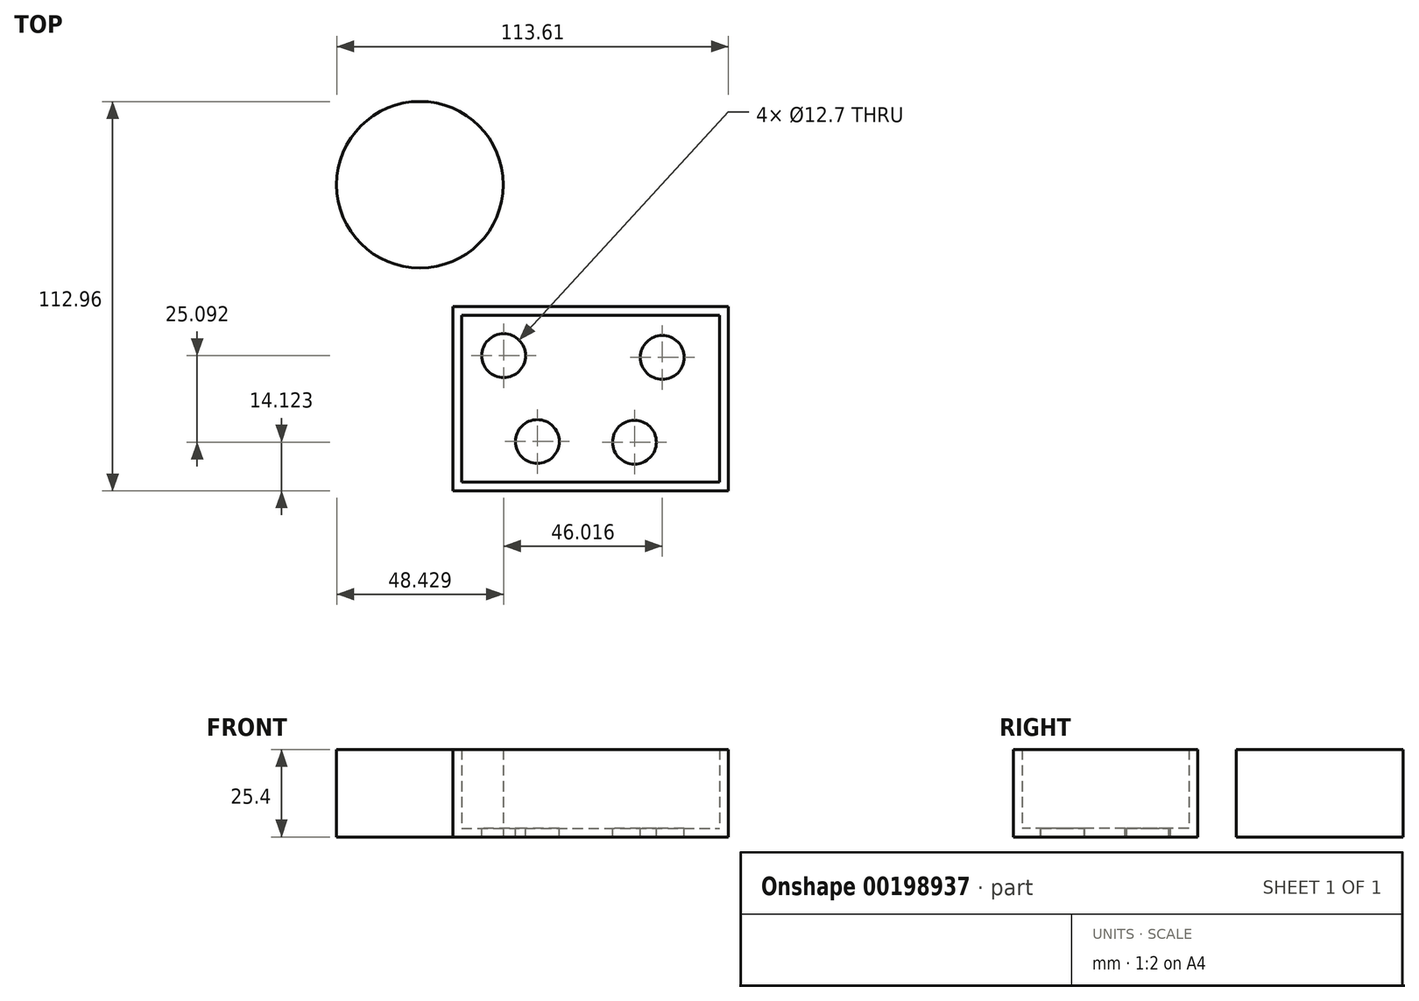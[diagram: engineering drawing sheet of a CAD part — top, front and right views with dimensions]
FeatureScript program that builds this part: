
annotation { "Feature Type Name" : "Feature", "Feature Type Description" : "" }
export const myFeature = defineFeature(function(context is Context, id is Id, definition is map)
    precondition{}
    {
        {
            var Q0;
            Q0=qCreatedBy(makeId("Top.planeOp"),FACE);
            var sketch = newSketch(context, id + "F0", { "sketchPlane" : qUnion([Q0])});
            skLineSegment(sketch, "E0.bottom", {"start": v(-40.26, 25.8) * mm, "end": v(39.65, 25.8) * mm});
            skLineSegment(sketch, "E0.top", {"start": v(-40.26, -27.61) * mm, "end": v(39.65, -27.61) * mm});
            skLineSegment(sketch, "E0.left", {"start": v(-40.26, 25.8) * mm, "end": v(-40.26, -27.61) * mm});
            skLineSegment(sketch, "E0.right", {"start": v(39.65, 25.8) * mm, "end": v(39.65, -27.61) * mm});
            skSolve(sketch);
        }
        {
            var Q0;
            Q0=makeQuery(id+"F0.imprint","IMPRINT",FACE,{"disambiguationData":[TD([[makeQuery(id+"F0.imprint","IMPRINT",EDGE,{"derivedFrom":sQuery(id+"F0.wireOp",EDGE,"E0.bottom")}),-1.0]])]});
            extrude(context, id + "F1", {"entities" : qUnion([Q0]), "depth" : 25.4 * mm});
        }
        {
            var Q0;
            Q0=makeQuery(id+"F1.opExtrude","CAP_FACE",FACE,{"disambiguationData":[OSD([sQuery(id+"F0.wireOp",EDGE,"E0.bottom"),sQuery(id+"F0.wireOp",EDGE,"E0.top"),sQuery(id+"F0.wireOp",EDGE,"E0.left"),sQuery(id+"F0.wireOp",EDGE,"E0.right")])],"isStart":false});
            shell(context, id + "F2", {"entities" : qUnion([Q0]), "thickness" : 2.54 * mm});
        }
        {
            var Q0;
            Q0=makeQuery(id+"F2.opShell","OFFSET_FACE",FACE,{"disambiguationData":[OSD([sQuery(id+"F0.wireOp",EDGE,"E0.bottom"),sQuery(id+"F0.wireOp",EDGE,"E0.top"),sQuery(id+"F0.wireOp",EDGE,"E0.left"),sQuery(id+"F0.wireOp",EDGE,"E0.right")])]});
            var sketch = newSketch(context, id + "F3", { "sketchPlane" : qUnion([Q0])});
            skPoint(sketch, "E1", {"position": v(-25.53, 11.6) * mm});
            skPoint(sketch, "E2", {"position": v(20.48, 11.1) * mm});
            skPoint(sketch, "E3", {"position": v(-15.75, -13.32) * mm});
            skPoint(sketch, "E4", {"position": v(12.4, -13.49) * mm});
            skSolve(sketch);
        }
        {
            var Q0;
            Q0=sQuery(id+"F3.wireOp",VERTEX,"E1");
            var Q1;
            Q1=sQuery(id+"F3.wireOp",VERTEX,"E2");
            var Q2;
            Q2=sQuery(id+"F3.wireOp",VERTEX,"E4");
            var Q3;
            Q3=sQuery(id+"F3.wireOp",VERTEX,"E3");
            var Q4;
            Q4=makeQuery(id+"F1.opExtrude","SWEPT_BODY",BODY,{"disambiguationData":[OSD([sQuery(id+"F0.wireOp",EDGE,"E0.bottom"),sQuery(id+"F0.wireOp",EDGE,"E0.top"),sQuery(id+"F0.wireOp",EDGE,"E0.left"),sQuery(id+"F0.wireOp",EDGE,"E0.right")])]});
            hole(context, id + "F4", {"style" : HoleStyle.SIMPLE, "endStyle" : HoleEndStyle.THROUGH, "holeDiameter" : 12.7 * mm, "locations" : qUnion([Q0, Q1, Q2, Q3]), "scope" : qUnion([Q4]), "isTappedThrough" : true});
        }
        {
            var Q0;
            Q0=qCreatedBy(makeId("Top.planeOp"),FACE);
            var sketch = newSketch(context, id + "F5", { "sketchPlane" : qUnion([Q0])});
            skCircle(sketch, "E5", {"center": v(-49.8, 61.19) * mm, "radius": 24.16 * mm});
            skSolve(sketch);
        }
        {
            var Q0;
            Q0=makeQuery(id+"F5.imprint","IMPRINT",FACE,{"disambiguationData":[TD([[makeQuery(id+"F5.imprint","IMPRINT",EDGE,{"derivedFrom":sQuery(id+"F5.wireOp",EDGE,"E5")}),1.0]])]});
            extrude(context, id + "F6", {"entities" : qUnion([Q0]), "depth" : 25.4 * mm});
        }
    });
